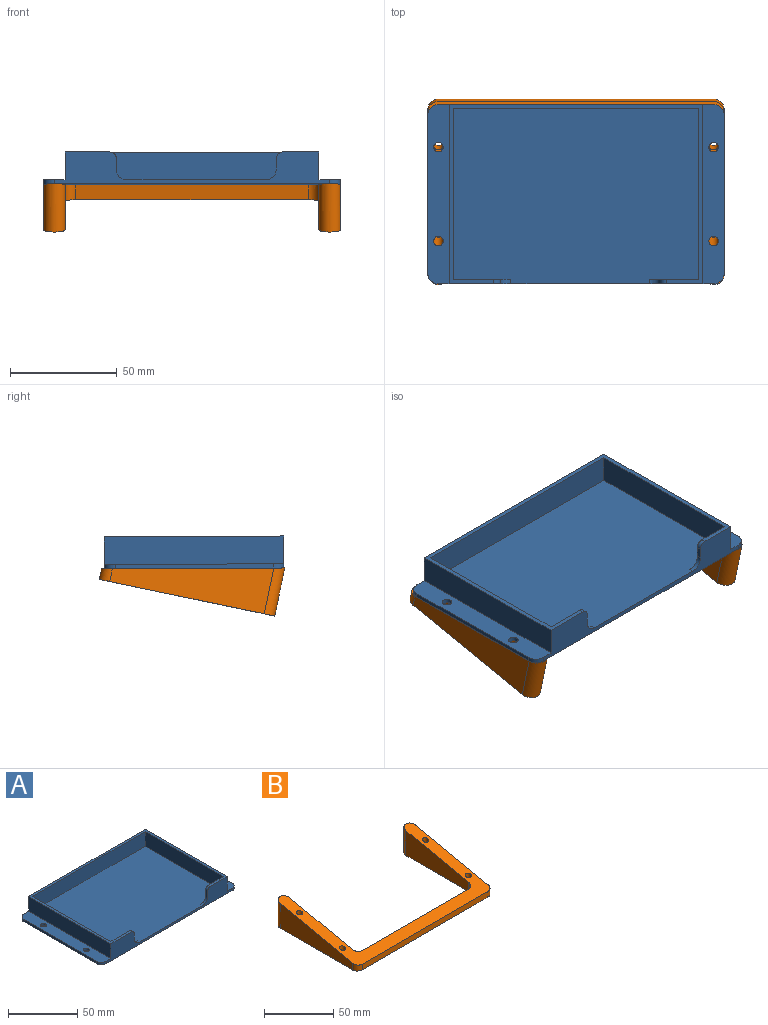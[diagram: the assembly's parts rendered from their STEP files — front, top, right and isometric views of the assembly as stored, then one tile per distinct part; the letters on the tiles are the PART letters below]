
ASSEMBLY  parts=2 mates=1
PART A: 30 faces, bbox 139x84x15 mm
  f0: plane 23x13mm, normal (0,1,0), area 237.4mm2, adj f2,f6,f11,f16,f19,f24
  f1: plane 129x15mm, normal (0,-1,0), area 836.9mm2, adj f2,f3,f4,f10,f11,f12,f14,f16
  f2: plane 119x84mm, normal (0,0,1), area 634mm2, adj f0,f1,f3,f5,f6,f7,f8,f9
  f3: plane 84x13mm, normal (1,0,0), area 1092mm2, adj f1,f2,f9,f14
  f4: plane 139x84mm, normal (0,0,-1), area 11590.9mm2, adj f1,f9,f13,f15,f20,f21,f22,f23
  f5: plane 27x13mm, normal (0,1,0), area 289.4mm2, adj f2,f8,f11,f17,f18,f25
  f6: plane 80x13mm, normal (-1,0,0), area 1040mm2, adj f0,f2,f7,f11
  f7: plane 115x13mm, normal (0,-1,0), area 1495mm2, adj f2,f6,f8,f11
  f8: plane 80x13mm, normal (1,0,0), area 1040mm2, adj f2,f5,f7,f11
  f9: plane 129x15mm, normal (0,1,0), area 1805mm2, adj f2,f3,f4,f10,f12,f14,f21,f22
  f10: plane 84x13mm, normal (-1,0,0), area 1092mm2, adj f1,f2,f9,f12
  f11: plane 115x82mm, normal (0,0,1), area 9330mm2, adj f0,f1,f5,f6,f7,f8,f18,f19
  f12: plane 84x10mm, normal (0,0,1), area 797.5mm2, adj f1,f9,f10,f13,f22,f23,f26,f27
  f13: plane 74x2mm, normal (-1,0,0), area 148mm2, adj f4,f12,f22,f23
  f14: plane 84x10mm, normal (0,0,1), area 797.5mm2, adj f1,f3,f9,f15,f20,f21,f28,f29
  f15: plane 74x2mm, normal (1,0,0), area 148mm2, adj f4,f14,f20,f21
  f16: plane 5x2mm, normal (-1,0,0), area 10mm2, adj f0,f1,f19,f24
  f17: plane 5x2mm, normal (1,0,0), area 10mm2, adj f1,f5,f18,f25
  f18: cylinder r=5mm len=5mm, axis (0,-1,0), area 15.7mm2, adj f1,f5,f11,f17
  f19: cylinder r=5mm len=5mm, axis (0,-1,0), area 15.7mm2, adj f0,f1,f11,f16
  f20: cylinder r=5mm len=5mm, axis (0,0,-1), area 15.7mm2, adj f1,f4,f14,f15
  f21: cylinder r=5mm len=5mm, axis (0,0,1), area 15.7mm2, adj f4,f9,f14,f15
  f22: cylinder r=5mm len=5mm, axis (0,0,1), area 15.7mm2, adj f4,f9,f12,f13
  f23: cylinder r=5mm len=5mm, axis (0,0,-1), area 15.7mm2, adj f1,f4,f12,f13
  f24: cylinder r=3mm len=3mm, axis (0,-1,0), area 9.4mm2, adj f0,f1,f2,f16
  f25: cylinder r=3mm len=3mm, axis (0,1,0), area 9.4mm2, adj f1,f2,f5,f17
  f26: cylinder r=2.25mm len=4.5mm, axis (0,0,1), area 28.3mm2, adj f4,f12
  f27: cylinder r=2.25mm len=4.5mm, axis (0,0,1), area 28.3mm2, adj f4,f12
  f28: cylinder r=2.25mm len=4.5mm, axis (0,0,1), area 28.3mm2, adj f4,f14
  f29: cylinder r=2.25mm len=4.5mm, axis (0,0,1), area 28.3mm2, adj f4,f14
PART B: 18 faces, bbox 139x84x23 mm
  f0: plane 74x21.93mm, normal (-1,0,0), area 1036mm2, adj f12,f13,f14,f15
  f1: plane 129x5mm, normal (0,-1,0), area 645mm2, adj f12,f13,f15,f16
  f2: cylinder r=5mm len=8.21mm, axis (0,0,-1), area 59.2mm2, adj f3,f10,f12,f13
  f3: plane 109x7.14mm, normal (0,1,0), area 778.6mm2, adj f2,f4,f12,f13
  f4: cylinder r=5mm len=8.21mm, axis (0,0,-1), area 59.2mm2, adj f3,f5,f12,f13
  f5: plane 64x21.93mm, normal (1,0,0), area 964.6mm2, adj f4,f12,f13,f14
  f6: plane 74x21.93mm, normal (1,0,0), area 1036mm2, adj f12,f13,f16,f17
  f7: cylinder r=2.25mm len=9.77mm, axis (0,0,-1), area 131.3mm2, adj f12,f13
  f8: cylinder r=2.25mm len=19.2mm, axis (0,0,-1), area 264.6mm2, adj f12,f13
  f9: cylinder r=2.25mm len=19.2mm, axis (0,0,-1), area 264.6mm2, adj f12,f13
  f10: plane 64x21.93mm, normal (-1,0,0), area 964.6mm2, adj f2,f12,f13,f17
  f11: cylinder r=2.25mm len=9.77mm, axis (0,0,-1), area 131.3mm2, adj f12,f13
  f12: plane 139x84mm, normal (0,0,-1), area 2784.9mm2, adj f0,f1,f2,f3,f4,f5,f6,f7
  f13: plane 139x84mm, normal (0,-0.21,0.98), area 2848.1mm2, adj f0,f1,f2,f3,f4,f5,f6,f7
  f14: cylinder r=5mm len=23mm, axis (0,0,1), area 355.2mm2, adj f0,f5,f12,f13
  f15: cylinder r=5mm len=6.07mm, axis (0,0,-1), area 42.3mm2, adj f0,f1,f12,f13
  f16: cylinder r=5mm len=6.07mm, axis (0,0,-1), area 42.3mm2, adj f1,f6,f12,f13
  f17: cylinder r=5mm len=23mm, axis (0,0,1), area 355.2mm2, adj f6,f10,f12,f13
PLACE A rot(axis=(-1,0,0),0.3deg) t=(-9.35,3.9,6.24)mm
PLACE B rot(axis=(0,-0.1,0.99),180deg) t=(-9.35,7.27,-7.47)mm
MATE planar B.f13 <-> A.f29  axis (0,0,1) through (55.15,-18.1,6.35)mm
